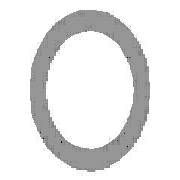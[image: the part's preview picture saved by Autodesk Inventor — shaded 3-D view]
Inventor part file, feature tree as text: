
AUTODESK INVENTOR PART (.ipt)
format: ipt  version: 2024.3 (Build 283343000, 343)  size: 119,808 bytes
history: native  units: mm (DEFAULTED — no unit token found)
features: other x4, sketch x1, plane x1
ambient origin geometry x8: Origin, YZ Plane, XZ Plane, XY Plane, X Axis, Y Axis, Z Axis, Center Point
bodies: Solid1 (feature_tree), Body (feature_tree)
feature tree (6):
  parser-record x1  (decoder bookkeeping rows leaked as tree rows — omitted from the tree; the rows remain in map.json)
  other  "Driven Length"
  other  "Start Plane"
  other  "End Plane"
  sketch  "Sketch3"  dims[d0=42.4mm d1=2.0mm d2=1100.0mm d3=0.0mm d4=-0.0mm d5=1100.0mm d6=90.0deg d7=1100.0mm]
  plane  "Work Plane3"
